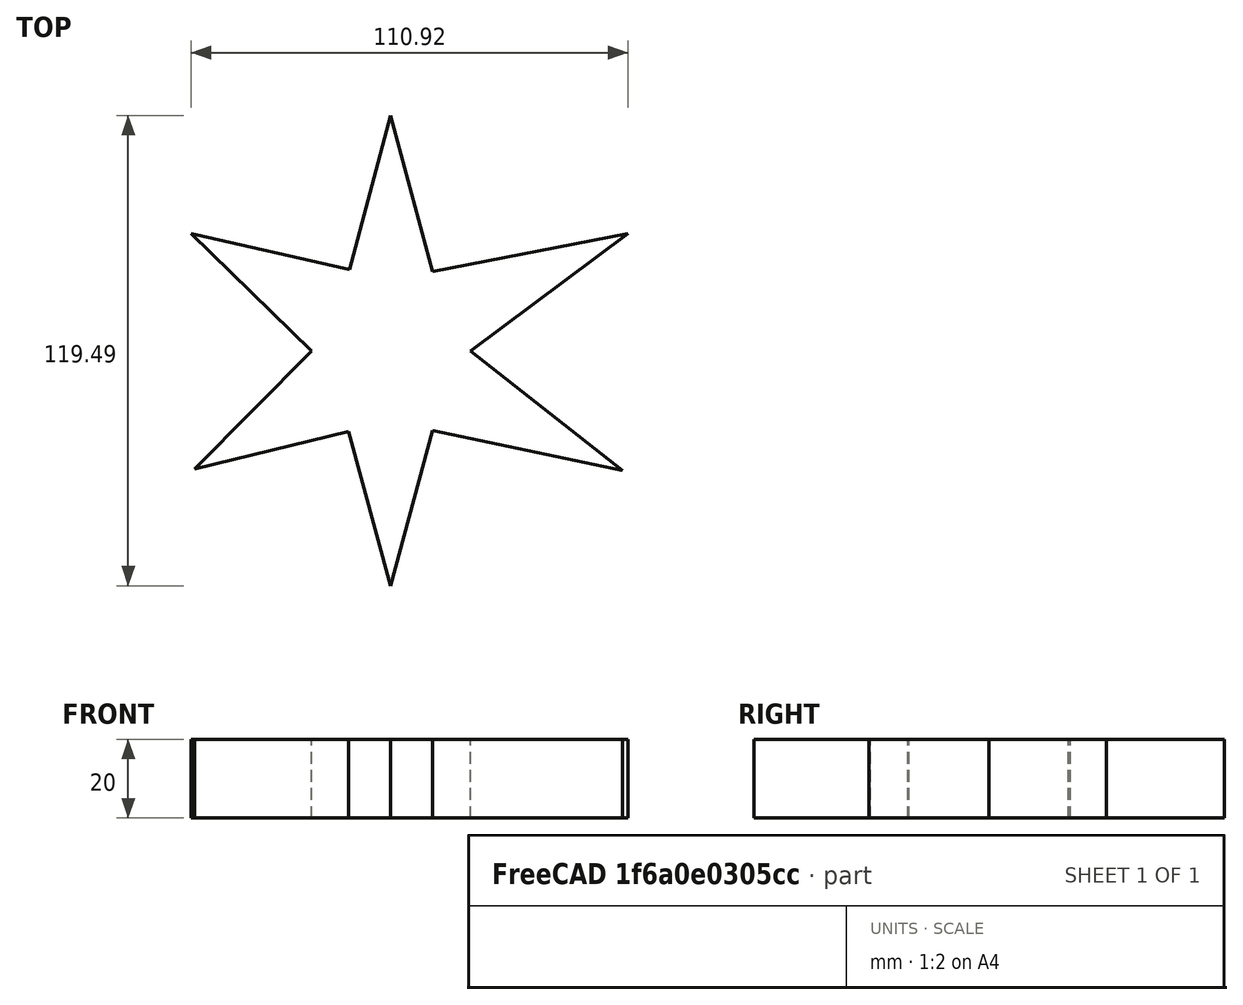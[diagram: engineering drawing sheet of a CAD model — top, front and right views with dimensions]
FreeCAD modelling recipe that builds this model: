
FCSTD DOCUMENT  (FreeCAD 1.0R39319 (Git))
Label: ojt1_t16p01_star
License: All rights reserved
LicenseURL: https://en.wikipedia.org/wiki/All_rights_reserved
objects: Sketcher::SketchObject×1, PartDesign::Pad×1, PartDesign::Body×1
note: 6 computed .brp shape members not serialized (recipe doc carries the construction recipe); baked Part::Feature solids carry a one-line shape summary decoded from their .brp

FEATURE [Sketcher::SketchObject] Sketch  label="esbós-estrella"
  ArcFitTolerance = 1e-06
  AttachmentSupport = -> [XY_Plane]
  FullyConstrained = false
  MakeInternals = false
  MapMode = 5
  sketch-geometry (12):
    g0: LineSegment StartX=1.8e-15 StartY=59.8247 StartZ=0 EndX=10.7399 EndY=20.2214 EndZ=0
    g1: LineSegment StartX=10.7399 StartY=20.2214 StartZ=0 EndX=60.3268 EndY=29.8777 EndZ=0
    g2: LineSegment StartX=60.3268 StartY=29.8777 StartZ=0 EndX=20.3154 EndY=0 EndZ=0
    g3: LineSegment StartX=20.3154 StartY=0 StartZ=0 EndX=58.9554 EndY=-30.3748 EndZ=0
    g4: LineSegment StartX=58.9554 StartY=-30.3748 StartZ=0 EndX=10.7399 EndY=-20.2311 EndZ=0
    g5: LineSegment StartX=10.7399 StartY=-20.2311 StartZ=0 EndX=1.8e-15 EndY=-59.6704 EndZ=0
    g6: LineSegment StartX=1.8e-15 StartY=-59.6704 StartZ=0 EndX=-10.6608 EndY=-20.4921 EndZ=0
    g7: LineSegment StartX=-10.6608 StartY=-20.4921 StartZ=0 EndX=-49.7465 EndY=-29.9894 EndZ=0
    g8: LineSegment StartX=-49.7465 StartY=-29.9894 StartZ=0 EndX=-20.0253 EndY=0 EndZ=0
    g9: LineSegment StartX=-20.0253 StartY=0 StartZ=0 EndX=-50.5913 EndY=29.8777 EndZ=0
    g10: LineSegment StartX=-50.5913 StartY=29.8777 StartZ=0 EndX=-10.3998 EndY=20.7433 EndZ=0
    g11: LineSegment StartX=-10.3998 StartY=20.7433 StartZ=0 EndX=1.8e-15 EndY=59.8247 EndZ=0
  constraints (16):
    c: PointOnObject(g0,g-2)
    c: Coincident(g0,g1)
    c: Coincident(g1,g2)
    c: PointOnObject(g2,g-1)
    c: Coincident(g2,g3)
    c: Coincident(g3,g4)
    c: Coincident(g4,g5)
    c: PointOnObject(g5,g-2)
    c: Coincident(g5,g6)
    c: Coincident(g6,g7)
    c: Coincident(g7,g8)
    c: PointOnObject(g8,g-1)
    c: Coincident(g8,g9)
    c: Coincident(g9,g10)
    c: Coincident(g10,g11)
    c: Coincident(g11,g0)
FEATURE [PartDesign::Pad] Pad  label="estrella"
  Direction = (0,0,1)
  Length = 20
  Length2 = 10
  Profile = -> Sketch
  ReferenceAxis = -> Sketch [N_Axis]
  Refine = true
  Suppressed = false
  Type = 0
FEATURE [PartDesign::Body] Body  label="Cos"
  AllowCompound = false
  Group = -> [Sketch,Pad]
  Origin = -> Origin
  Tip = -> Pad
